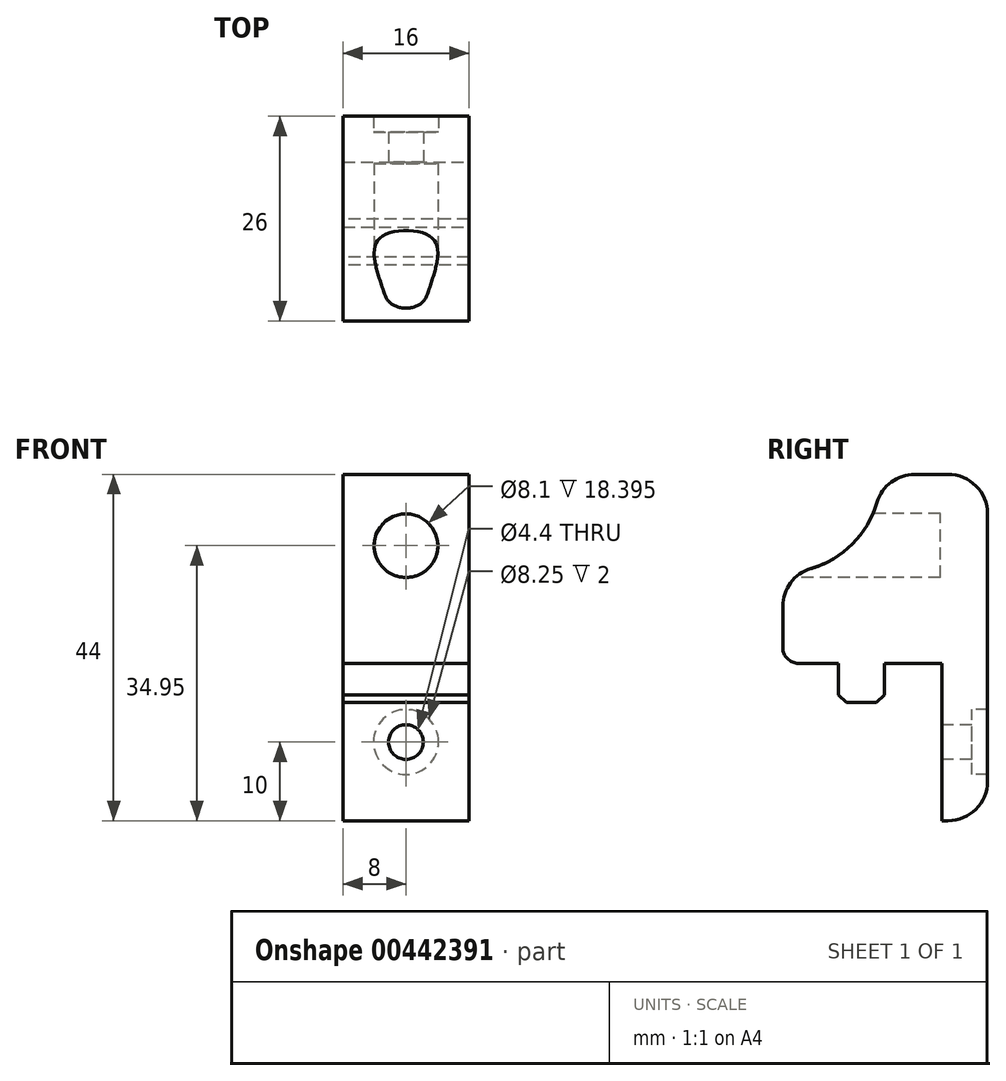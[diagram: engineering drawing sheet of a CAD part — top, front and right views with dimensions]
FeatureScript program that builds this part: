
annotation { "Feature Type Name" : "Feature", "Feature Type Description" : "" }
export const myFeature = defineFeature(function(context is Context, id is Id, definition is map)
    precondition{}
    {
        {
            var Q0;
            Q0=qCreatedBy(makeId("Front.planeOp"),FACE);
            var sketch = newSketch(context, id + "F0", { "sketchPlane" : qUnion([Q0])});
            skLineSegment(sketch, "E0.bottom", {"start": v(8, -12) * mm, "end": v(-8, -12) * mm});
            skLineSegment(sketch, "E0.top", {"start": v(8, 12) * mm, "end": v(-8, 12) * mm});
            skLineSegment(sketch, "E0.left", {"start": v(8, -12) * mm, "end": v(8, 12) * mm});
            skLineSegment(sketch, "E0.right", {"start": v(-8, -12) * mm, "end": v(-8, 12) * mm});
            skPoint(sketch, "E0.middle", {"position": v(0, 0) * mm});
            skSolve(sketch);
        }
        {
            var Q0;
            Q0=qSketchRegion(id+"F0",true);
            extrude(context, id + "F1", {"entities" : qUnion([Q0]), "depth" : 26 * mm, "offsetDistance" : 25 * mm, "symmetric" : true});
        }
        {
            var Q0;
            Q0=makeQuery(id+"F1.opExtrude","SWEPT_FACE",FACE,{"disambiguationData":[OSD([sQuery(id+"F0.wireOp",EDGE,"E0.bottom")])]});
            var sketch = newSketch(context, id + "F2", { "sketchPlane" : qUnion([Q0])});
            skLineSegment(sketch, "E1.bottom", {"start": v(8, 0.1) * mm, "end": v(-8, 0.1) * mm});
            skLineSegment(sketch, "E1.top", {"start": v(8, 5.9) * mm, "end": v(-8, 5.9) * mm});
            skLineSegment(sketch, "E1.left", {"start": v(8, 0.1) * mm, "end": v(8, 5.9) * mm});
            skLineSegment(sketch, "E1.right", {"start": v(-8, 0.1) * mm, "end": v(-8, 5.9) * mm});
            skPoint(sketch, "E1.middle", {"position": v(0, 3) * mm});
            skLineSegment(sketch, "E2.bottom", {"start": v(-8, -13) * mm, "end": v(8, -13) * mm});
            skLineSegment(sketch, "E2.top", {"start": v(-8, -7.2) * mm, "end": v(8, -7.2) * mm});
            skLineSegment(sketch, "E2.left", {"start": v(-8, -13) * mm, "end": v(-8, -7.2) * mm});
            skLineSegment(sketch, "E2.right", {"start": v(8, -13) * mm, "end": v(8, -7.2) * mm});
            skSolve(sketch);
        }
        {
            var Q0;
            Q0=makeQuery(id+"F2.imprint","IMPRINT",FACE,{"disambiguationData":[TD([[makeQuery(id+"F2.imprint","IMPRINT",EDGE,{"derivedFrom":sQuery(id+"F2.wireOp",EDGE,"E1.bottom")}),-1.0]])]});
            extrude(context, id + "F3", {"entities" : qUnion([Q0]), "operationType" : NewBodyOperationType.ADD, "depth" : 5 * mm, "offsetDistance" : 25 * mm});
        }
        {
            var Q0;
            Q0=makeQuery(id+"F2.imprint","IMPRINT",FACE,{"disambiguationData":[TD([[makeQuery(id+"F2.imprint","IMPRINT",EDGE,{"derivedFrom":sQuery(id+"F2.wireOp",EDGE,"E2.bottom")}),-1.0]])]});
            extrude(context, id + "F4", {"entities" : qUnion([Q0]), "operationType" : NewBodyOperationType.ADD, "depth" : 20 * mm, "offsetDistance" : 25 * mm});
        }
        {
            var Q0;
            Q0=makeQuery(id+"F1.opExtrude","CAP_FACE",FACE,{"disambiguationData":[OSD([sQuery(id+"F0.wireOp",EDGE,"E0.bottom"),sQuery(id+"F0.wireOp",EDGE,"E0.top"),sQuery(id+"F0.wireOp",EDGE,"E0.left"),sQuery(id+"F0.wireOp",EDGE,"E0.right")])],"isStart":false});
            var sketch = newSketch(context, id + "F5", { "sketchPlane" : qUnion([Q0])});
            skCircle(sketch, "E3", {"center": v(0, 2.95) * mm, "radius": 4.05 * mm});
            skSolve(sketch);
        }
        {
            var Q0;
            Q0=makeQuery(id+"F5.imprint","IMPRINT",FACE,{"disambiguationData":[TD([[makeQuery(id+"F5.imprint","IMPRINT",EDGE,{"derivedFrom":sQuery(id+"F5.wireOp",EDGE,"E3")}),1.0]])]});
            var Q1;
            Q1=makeQuery(id+"F4.boolean.opBoolean","MERGE",FACE,{"derivedFrom":[makeQuery(id+"F1.opExtrude","CAP_FACE",FACE,{"disambiguationData":[OSD([sQuery(id+"F0.wireOp",EDGE,"E0.bottom"),sQuery(id+"F0.wireOp",EDGE,"E0.top"),sQuery(id+"F0.wireOp",EDGE,"E0.left"),sQuery(id+"F0.wireOp",EDGE,"E0.right")])],"isStart":true}),makeQuery(id+"F4.opExtrude","SWEPT_FACE",FACE,{"disambiguationData":[OSD([sQuery(id+"F2.wireOp",EDGE,"E2.bottom")])]})]});
            extrude(context, id + "F6", {"entities" : qUnion([Q0]), "operationType" : NewBodyOperationType.REMOVE, "oppositeDirection" : true, "depth" : 20 * mm, "offsetDistance" : 25 * mm});
        }
        {
            var Q0;
            Q0=makeQuery(id+"F4.boolean.opBoolean","MERGE",FACE,{"derivedFrom":[makeQuery(id+"F1.opExtrude","CAP_FACE",FACE,{"disambiguationData":[OSD([sQuery(id+"F0.wireOp",EDGE,"E0.bottom"),sQuery(id+"F0.wireOp",EDGE,"E0.top"),sQuery(id+"F0.wireOp",EDGE,"E0.left"),sQuery(id+"F0.wireOp",EDGE,"E0.right")])],"isStart":true}),makeQuery(id+"F4.opExtrude","SWEPT_FACE",FACE,{"disambiguationData":[OSD([sQuery(id+"F2.wireOp",EDGE,"E2.bottom")])]})]});
            var sketch = newSketch(context, id + "F7", { "sketchPlane" : qUnion([Q0])});
            skLineSegment(sketch, "E4", {"start": v(-8, -22) * mm, "end": v(8, -22) * mm, "construction": true});
            skPoint(sketch, "E5", {"position": v(0, -22) * mm});
            skSolve(sketch);
        }
        {
            var Q0;
            Q0=sQuery(id+"F7.wireOp",VERTEX,"E5");
            var Q1;
            Q1=sQuery(id+"F7.wireOp",VERTEX,"7c64e804-d5a0-4580-aa40-0e1040ca2d0c0.MirrorP");
            var Q2;
            Q2=makeQuery(id+"F1.opExtrude","SWEPT_BODY",BODY,{"disambiguationData":[OSD([sQuery(id+"F0.wireOp",EDGE,"E0.bottom"),sQuery(id+"F0.wireOp",EDGE,"E0.top"),sQuery(id+"F0.wireOp",EDGE,"E0.left"),sQuery(id+"F0.wireOp",EDGE,"E0.right")])]});
            hole(context, id + "F8", {"style" : HoleStyle.C_BORE, "endStyle" : HoleEndStyle.THROUGH, "holeDiameter" : 4.4 * mm, "cBoreDiameter" : 8.25 * mm, "cBoreDepth" : 2 * mm, "majorDiameter" : 5 * mm, "isTappedThrough" : true, "tappedDepth" : 12 * mm, "tapClearance" : 3, "locations" : qUnion([Q0, Q1]), "scope" : qUnion([Q2])});
        }
        {
            var Q0;
            Q0=makeQuery(id+"F3.opExtrude","CAP_EDGE",EDGE,{"disambiguationData":[OSD([sQuery(id+"F2.wireOp",EDGE,"E1.top")])],"isStart":false});
            var Q1;
            Q1=makeQuery(id+"F3.opExtrude","CAP_EDGE",EDGE,{"disambiguationData":[OSD([sQuery(id+"F2.wireOp",EDGE,"E1.bottom")])],"isStart":false});
            chamfer(context, id + "F9", {"entities" : qUnion([Q0, Q1]), "width" : 1 * mm, "tangentPropagation" : true});
        }
        {
            var Q0;
            Q0=makeQuery(id+"F4.boolean.opBoolean","MERGE",FACE,{"derivedFrom":[makeQuery(id+"F3.boolean.opBoolean","MERGE",FACE,{"derivedFrom":[makeQuery(id+"F1.opExtrude","SWEPT_FACE",FACE,{"disambiguationData":[OSD([sQuery(id+"F0.wireOp",EDGE,"E0.left")])]}),makeQuery(id+"F3.opExtrude","SWEPT_FACE",FACE,{"disambiguationData":[OSD([sQuery(id+"F2.wireOp",EDGE,"E1.left")])]})]}),makeQuery(id+"F4.opExtrude","SWEPT_FACE",FACE,{"disambiguationData":[OSD([sQuery(id+"F2.wireOp",EDGE,"E2.right")])]})]});
            var sketch = newSketch(context, id + "F10", { "sketchPlane" : qUnion([Q0])});
            skCircle(sketch, "E6", {"center": v(-13, 12) * mm, "radius": 12.5 * mm});
            skSolve(sketch);
        }
        {
            var Q0;
            {var subQ0=sQuery(id+"F10.wireOp",EDGE,"E6");var subQ1=sQuery(id+"F0.wireOp",EDGE,"E0.left");var subQ2=makeQuery(id+"F1.opExtrude","SWEPT_EDGE",EDGE,{"disambiguationData":[OSD([sQuery(id+"F0.wireOp",EDGE,"E0.top"),subQ1])]});var subQ3=makeQuery(id+"F10.imprint","INTERSECT",VERTEX,{"derivedFrom":[subQ2,subQ0]});Q0=makeQuery(id+"F10.imprint","IMPRINT",FACE,{"disambiguationData":[TD([[makeQuery(id+"F10.imprint","IMPRINT",EDGE,{"disambiguationData":[TD([[subQ3,-1.0]])],"derivedFrom":subQ0}),1.0]])]});}
            var Q1;
            {var subQ0=sQuery(id+"F10.wireOp",EDGE,"E6");var subQ1=sQuery(id+"F0.wireOp",EDGE,"E0.left");var subQ4=makeQuery(id+"F1.opExtrude","CAP_EDGE",EDGE,{"disambiguationData":[OSD([subQ1])],"isStart":false});var subQ5=makeQuery(id+"F10.imprint","INTERSECT",VERTEX,{"derivedFrom":[subQ4,subQ0]});Q1=makeQuery(id+"F10.imprint","IMPRINT",FACE,{"disambiguationData":[TD([[makeQuery(id+"F10.imprint","IMPRINT",EDGE,{"disambiguationData":[TD([[subQ5,-1.0]])],"derivedFrom":subQ0}),1.0]])]});}
            extrude(context, id + "F11", {"entities" : qUnion([Q0, Q1]), "operationType" : NewBodyOperationType.REMOVE, "endBound" : BoundingType.THROUGH_ALL, "oppositeDirection" : true, "depth" : 25 * mm, "offsetDistance" : 25 * mm});
        }
        {
            var Q0;
            {var subQ0=sQuery(id+"F2.wireOp",EDGE,"E2.bottom");var subQ1=sQuery(id+"F0.wireOp",EDGE,"E0.left");var subQ2=sQuery(id+"F2.wireOp",EDGE,"E2.right");var subQ3=sQuery(id+"F10.wireOp",EDGE,"E6");Q0=makeQuery(id+"F11.boolean.opBoolean","COPY",EDGE,{"disambiguationData":[TD([makeQuery(id+"F1.opExtrude","SWEPT_FACE",FACE,{"disambiguationData":[OSD([subQ1])]})])],"derivedFrom":makeQuery(id+"F11.opExtrude","SWEPT_EDGE",EDGE,{"disambiguationData":[OSD([subQ1,subQ0,subQ2,subQ3])]})});}
            var Q1;
            {var subQ0=sQuery(id+"F2.wireOp",EDGE,"E2.bottom");var subQ1=sQuery(id+"F0.wireOp",EDGE,"E0.right");var subQ2=sQuery(id+"F0.wireOp",EDGE,"E0.left");var subQ3=sQuery(id+"F10.wireOp",EDGE,"E6");Q1=makeQuery(id+"F11.boolean.opBoolean","COPY",EDGE,{"disambiguationData":[TD([makeQuery(id+"F1.opExtrude","SWEPT_FACE",FACE,{"disambiguationData":[OSD([subQ1])]})])],"derivedFrom":makeQuery(id+"F11.opExtrude","SWEPT_EDGE",EDGE,{"disambiguationData":[OSD([subQ2,subQ0,sQuery(id+"F2.wireOp",EDGE,"E2.right"),subQ3])]})});}
            var Q2;
            Q2=makeQuery(id+"F11.boolean.opBoolean","COPY",EDGE,{"derivedFrom":makeQuery(id+"F11.opExtrude","SWEPT_EDGE",EDGE,{"disambiguationData":[OSD([sQuery(id+"F0.wireOp",EDGE,"E0.top"),sQuery(id+"F0.wireOp",EDGE,"E0.left"),sQuery(id+"F10.wireOp",EDGE,"E6")])]})});
            var Q3;
            Q3=makeQuery(id+"F1.opExtrude","CAP_EDGE",EDGE,{"disambiguationData":[OSD([sQuery(id+"F0.wireOp",EDGE,"E0.top")])],"isStart":false});
            var Q4;
            Q4=makeQuery(id+"F4.opExtrude","CAP_EDGE",EDGE,{"disambiguationData":[OSD([sQuery(id+"F2.wireOp",EDGE,"E2.bottom")])],"isStart":false});
            var Q5;
            Q5=makeQuery(id+"F1.opExtrude","CAP_EDGE",EDGE,{"disambiguationData":[OSD([sQuery(id+"F0.wireOp",EDGE,"E0.top")])],"isStart":true});
            var Q6;
            Q6=makeQuery(id+"F11.boolean.opBoolean","INTERSECT",EDGE,{"derivedFrom":[makeQuery(id+"F1.opExtrude","SWEPT_FACE",FACE,{"disambiguationData":[OSD([sQuery(id+"F0.wireOp",EDGE,"E0.top")])]}),makeQuery(id+"F11.opExtrude","SWEPT_FACE",FACE,{"disambiguationData":[OSD([sQuery(id+"F10.wireOp",EDGE,"E6")])]})]});
            var Q7;
            Q7=makeQuery(id+"F11.boolean.opBoolean","INTERSECT",EDGE,{"disambiguationData":[OD(0.0)],"derivedFrom":[makeQuery(id+"F1.opExtrude","CAP_FACE",FACE,{"disambiguationData":[OSD([sQuery(id+"F0.wireOp",EDGE,"E0.bottom"),sQuery(id+"F0.wireOp",EDGE,"E0.top"),sQuery(id+"F0.wireOp",EDGE,"E0.left"),sQuery(id+"F0.wireOp",EDGE,"E0.right")])],"isStart":false}),makeQuery(id+"F11.opExtrude","SWEPT_FACE",FACE,{"disambiguationData":[OSD([sQuery(id+"F10.wireOp",EDGE,"E6")])]})]});
            fillet(context, id + "F12", {"entities" : qUnion([Q0, Q1, Q2, Q3, Q4, Q5, Q6, Q7]), "radius" : 5 * mm, "tangentPropagation" : true, "allowEdgeOverflow" : false});
        }
        {
            var Q0;
            Q0=makeQuery(id+"F1.opExtrude","CAP_EDGE",EDGE,{"disambiguationData":[OSD([sQuery(id+"F0.wireOp",EDGE,"E0.bottom")])],"isStart":false});
            fillet(context, id + "F13", {"entities" : qUnion([Q0]), "radius" : 2 * mm, "tangentPropagation" : true, "allowEdgeOverflow" : false});
        }
    });
